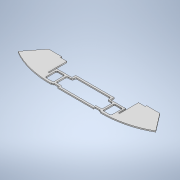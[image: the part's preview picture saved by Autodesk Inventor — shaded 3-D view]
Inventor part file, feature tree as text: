
AUTODESK INVENTOR PART (.ipt)
format: ipt  version: 2020.3 (Build 243373010, 373A)  size: 255,488 bytes
history: native  units: in
note: dims shown in document units (in); Inventor stores cm internally (conversion verified against a paired STEP export)
features: other x4, extrude x1, mirror x1, sketch x1
ambient origin geometry x8: Origin, YZ Plane, XZ Plane, XY Plane, X Axis, Y Axis, Z Axis, Center Point
bodies: Solid1 (feature_tree)
feature tree (7):
  other  "bulkhead_main"
  other  "base_sketch.ipt"
  extrude  "Extrusion1"  Depth=0.0787in
  mirror  "Mirror1"
  other  "stringer"
  other  "bulkhead_main_plane"
  sketch  "Sketch3"  dims[d0=0.3937in d1=0.0787in d2=0.0787in d3=0.0in d4=0.1181in d6=0.1181in d7=0.1181in d8=0.0787in d12=0.1181in d13=0.1181in d14=0.0787in d24=0.1969in d27=0.0079in d28=0.0787in d29=0.1181in d33=0.0472in d34=0.0472in d35=0.2362in d36=0.2362in d37=0.1181in d38=0.1181in d39=0.7902in]
